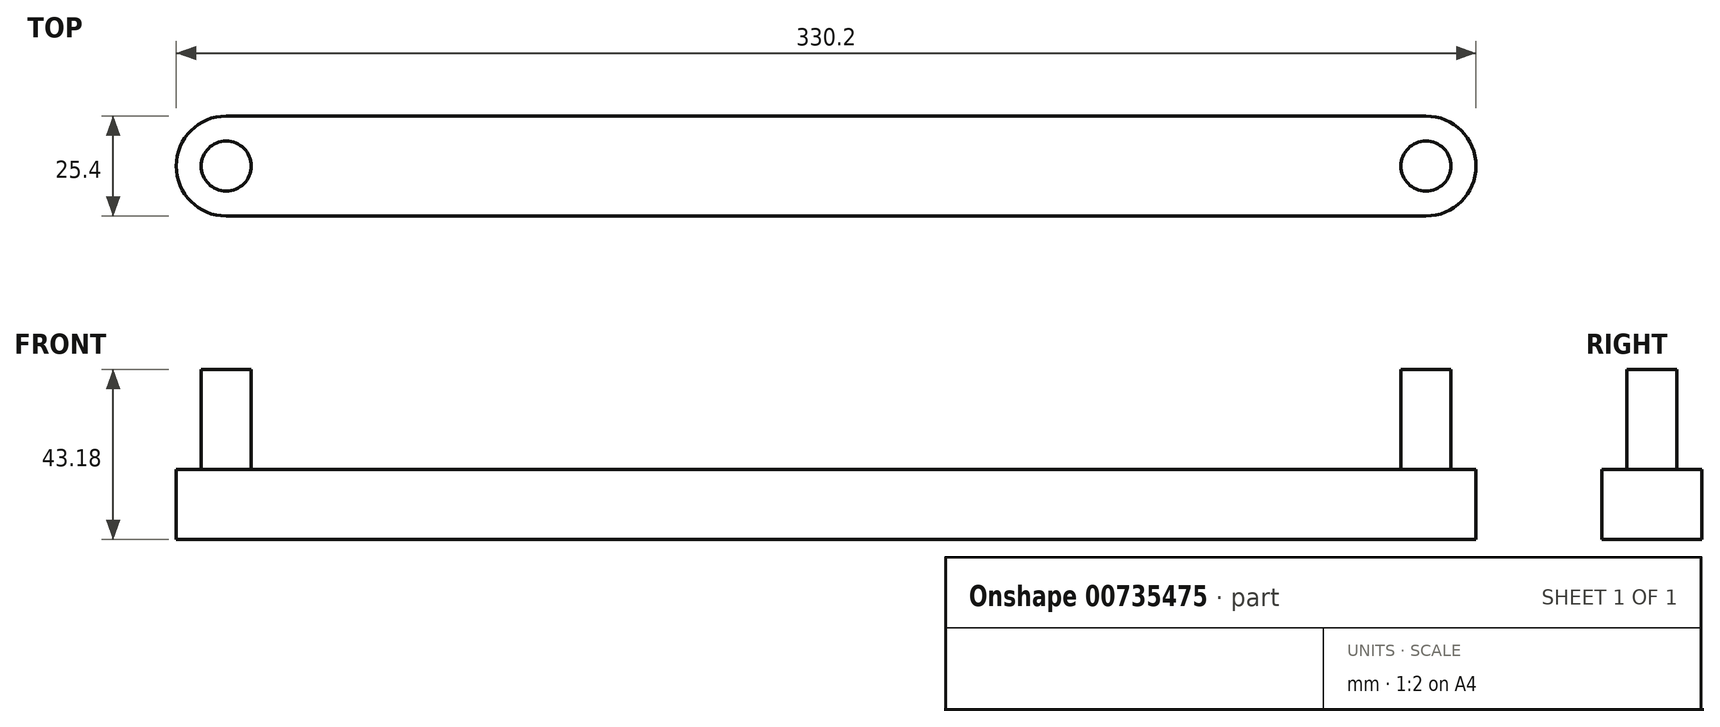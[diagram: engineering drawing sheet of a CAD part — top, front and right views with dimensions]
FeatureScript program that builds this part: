
annotation { "Feature Type Name" : "Feature", "Feature Type Description" : "" }
export const myFeature = defineFeature(function(context is Context, id is Id, definition is map)
    precondition{}
    {
        {
            var Q0;
            Q0=qCreatedBy(makeId("Top.planeOp"),FACE);
            var sketch = newSketch(context, id + "F0", { "sketchPlane" : qUnion([Q0])});
            skLineSegment(sketch, "E0", {"start": v(-170.86, 42.34) * mm, "end": v(133.94, 42.34) * mm});
            skLineSegment(sketch, "E1", {"start": v(133.94, 16.94) * mm, "end": v(-170.86, 16.94) * mm});
            skArc(sketch, "E2", {"start": v(-170.86, 42.34) * mm, "mid": v(-183.56, 29.64) * mm, "end": v(-170.86, 16.94) * mm});
            skArc(sketch, "E3", {"start": v(133.94, 42.34) * mm, "mid": v(146.64, 29.64) * mm, "end": v(133.94, 16.94) * mm});
            skSolve(sketch);
        }
        {
            var Q0;
            Q0=makeQuery(id+"F0.imprint","IMPRINT",FACE,{"disambiguationData":[TD([[makeQuery(id+"F0.imprint","IMPRINT",EDGE,{"derivedFrom":sQuery(id+"F0.wireOp",EDGE,"E0")}),-1.0]])]});
            extrude(context, id + "F1", {"entities" : qUnion([Q0]), "depth" : 17.78 * mm, "offsetDistance" : 25.4 * mm});
        }
        {
            var Q0;
            Q0=makeQuery(id+"F1.opExtrude","CAP_FACE",FACE,{"disambiguationData":[OSD([sQuery(id+"F0.wireOp",EDGE,"E0"),sQuery(id+"F0.wireOp",EDGE,"E1"),sQuery(id+"F0.wireOp",EDGE,"E2"),sQuery(id+"F0.wireOp",EDGE,"E3")])],"isStart":false});
            var sketch = newSketch(context, id + "F2", { "sketchPlane" : qUnion([Q0])});
            skCircle(sketch, "E4", {"center": v(-170.86, 29.64) * mm, "radius": 6.35 * mm});
            skCircle(sketch, "E5", {"center": v(133.94, 29.64) * mm, "radius": 6.35 * mm});
            skSolve(sketch);
        }
        {
            var Q0;
            Q0=makeQuery(id+"F2.imprint","IMPRINT",FACE,{"disambiguationData":[TD([[makeQuery(id+"F2.imprint","IMPRINT",EDGE,{"derivedFrom":sQuery(id+"F2.wireOp",EDGE,"E5")}),1.0]])]});
            var Q1;
            Q1=makeQuery(id+"F2.imprint","IMPRINT",FACE,{"disambiguationData":[TD([[makeQuery(id+"F2.imprint","IMPRINT",EDGE,{"derivedFrom":sQuery(id+"F2.wireOp",EDGE,"E4")}),1.0]])]});
            extrude(context, id + "F3", {"entities" : qUnion([Q0, Q1]), "operationType" : NewBodyOperationType.ADD, "depth" : 25.4 * mm, "offsetDistance" : 25.4 * mm});
        }
    });
